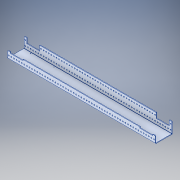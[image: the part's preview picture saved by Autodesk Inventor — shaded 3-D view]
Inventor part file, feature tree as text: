
AUTODESK INVENTOR PART (.ipt)
format: ipt  version: 2017 (Build 210142000, 142)  size: 361,984 bytes
history: native  units: in
note: dims shown in document units (in); Inventor stores cm internally (conversion verified against a paired STEP export)
features: other x5, reference x2, extrude x1, chamfer x1, sketch x1
ambient origin geometry x8: Origin, YZ Plane, XZ Plane, XY Plane, X Axis, Y Axis, Z Axis, Center Point
bodies: Solid1 (feature_tree)
feature tree (10):
  extrude  "Extrusion1"  Depth=0.5in
  chamfer  "Chamfer1"  Distance=3.0in
  sketch  "Sketch1"  dims[d0=1.0in d1=0.0in d2=0.5in d3=3.0in d4=1.0in d5=28.0in d6=2.5in d7=0.125in d8=0.125in d9=45.0deg]
  reference  "Reference1"
  reference  "Reference2"
  other  "LPattern4"
  other  "<userpath>\Documents\Inventor\2017 Robot\Robot Chassis.iam"
  other  "Robot Chassis.iam"
  other  "am-2951a_AM14U3_Outside_Plate:1"
  other  "am-2952a_AM14U3_Inside_Plate:1"
